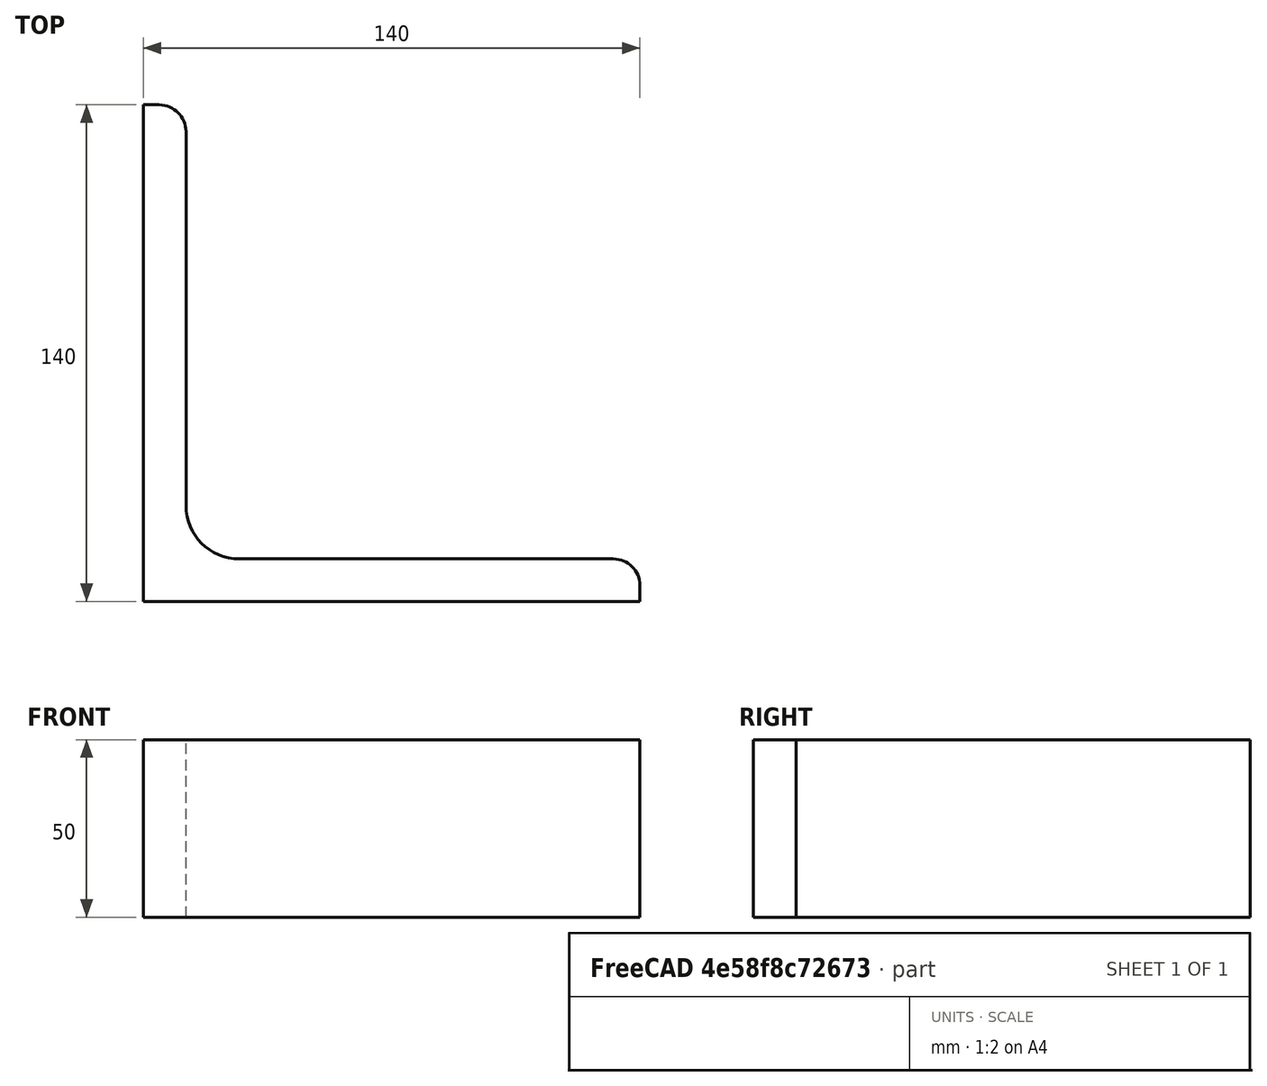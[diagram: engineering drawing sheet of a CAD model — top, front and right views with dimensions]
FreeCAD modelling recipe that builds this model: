
FCSTD DOCUMENT  (FreeCAD 0.15R4671 (Git))
Label: Angle Bar L140x140x12 EN10056 S235JR
License: All rights reserved
LicenseURL: http://en.wikipedia.org/wiki/All_rights_reserved
objects: Sketcher::SketchObject×1, Part::Extrusion×1
note: 2 computed .brp shape members not serialized (recipe doc carries the construction recipe); baked Part::Feature solids carry a one-line shape summary decoded from their .brp

FEATURE [Sketcher::SketchObject] Sketch
  sketch-geometry (9):
    g0: LineSegment StartX=0 StartY=0 StartZ=0 EndX=140 EndY=0 EndZ=0
    g1: LineSegment StartX=140 StartY=0 StartZ=0 EndX=140 EndY=4.5 EndZ=0
    g2: LineSegment StartX=132.5 StartY=12 StartZ=0 EndX=27 EndY=12 EndZ=0
    g3: LineSegment StartX=0 StartY=0 StartZ=0 EndX=0 EndY=140 EndZ=0
    g4: LineSegment StartX=0 StartY=140 StartZ=0 EndX=4.5 EndY=140 EndZ=0
    g5: LineSegment StartX=12 StartY=132.5 StartZ=0 EndX=12 EndY=27 EndZ=0
    g6: ArcOfCircle CenterX=27 CenterY=27 CenterZ=0 NormalX=0 NormalY=0 NormalZ=1 Radius=15 StartAngle=3.14159 EndAngle=4.71239
    g7: ArcOfCircle CenterX=4.5 CenterY=132.5 CenterZ=0 NormalX=0 NormalY=0 NormalZ=1 Radius=7.5 StartAngle=0 EndAngle=1.5708
    g8: ArcOfCircle CenterX=132.5 CenterY=4.5 CenterZ=0 NormalX=0 NormalY=0 NormalZ=1 Radius=7.5 StartAngle=0 EndAngle=1.5708
  constraints (23):
    c: Coincident(g0,g-1)
    c: Horizontal(g0)
    c: Coincident(g1,g0)
    c: Vertical(g1)
    c: Horizontal(g2)
    c: Coincident(g3,g-1)
    c: Vertical(g3)
    c: Coincident(g4,g3)
    c: Horizontal(g4)
    c: Vertical(g5)
    c: Tangent(g5,g6) = -1.5708
    c: Tangent(g2,g6) = 1.5708
    c: Tangent(g4,g7) = 1.5708
    c: Tangent(g5,g7) = 1.5708
    c: Tangent(g2,g8) = -1.5708
    c: Tangent(g1,g8) = -1.5708
    c: DistanceX(g0) = 140
    c: DistanceY(g3) = 140
    c: DistanceY(g0,g2) = 12
    c: DistanceX(g3,g5) = 12
    c: Radius(g6) = 15
    c: Radius(g8) = 7.5
    c: Radius(g7) = 7.5
FEATURE [Part::Extrusion] Extrude  label="Angle Bar L140x140x12 EN10056 S235JR"
  Base = -> Sketch
  Dir = (0,0,50)
  Solid = true
